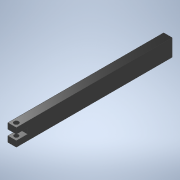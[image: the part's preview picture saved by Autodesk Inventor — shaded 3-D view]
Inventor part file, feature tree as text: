
AUTODESK INVENTOR PART (.ipt)
format: ipt  version: 2020.1 (Build 241239000, 239)  size: 129,024 bytes
history: native  units: in
note: dims shown in document units (in); Inventor stores cm internally (conversion verified against a paired STEP export)
features: extrude x4, sketch x4, projected_geometry x1
ambient origin geometry x8: Origin, YZ Plane, XZ Plane, XY Plane, X Axis, Y Axis, Z Axis, Center Point
bodies: Solid1 (feature_tree)
feature tree (9):
  extrude  "Extrusion1"  Depth=6.875in
  extrude  "Extrusion2"  Depth=0.25in
  extrude  "Extrusion3"  Depth=0.5in TaperAngle=0.0deg
  extrude  "Extrusion4"  Depth=0.1875in
  sketch  "Sketch1"  dims[d0=0.75in d1=6.875in]
  sketch  "Sketch2"  dims[d2=0.375in d3=0.0in d4=0.25in]
  sketch  "Sketch3"  dims[d5=0.5in d6=1.0in d7=0.0in]
  sketch  "Sketch4"  dims[d8=0.205in d9=0.1875in d10=0.25in d11=0.0in d12=0.1875in d13=1.0in d14=0.0in]
  projected_geometry  "Projected Loop1"
